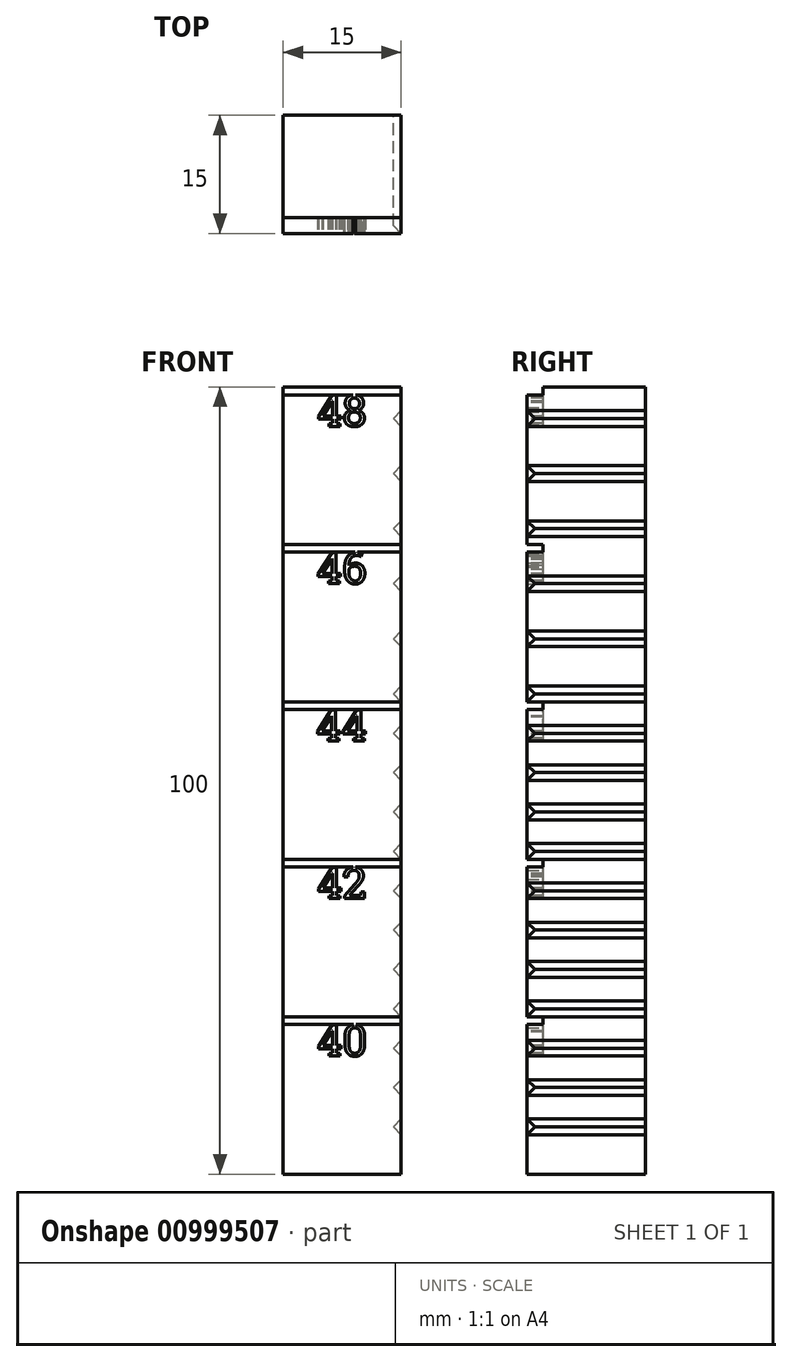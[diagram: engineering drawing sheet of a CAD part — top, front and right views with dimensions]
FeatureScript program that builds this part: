
annotation { "Feature Type Name" : "Feature", "Feature Type Description" : "" }
export const myFeature = defineFeature(function(context is Context, id is Id, definition is map)
    precondition{}
    {
        {
            var Q0;
            Q0=qCreatedBy(makeId("Top.planeOp"),FACE);
            var sketch = newSketch(context, id + "F0", { "sketchPlane" : qUnion([Q0])});
            skLineSegment(sketch, "E0.bottom", {"start": v(7.5, 7.5) * mm, "end": v(-7.5, 7.5) * mm});
            skLineSegment(sketch, "E0.top", {"start": v(7.5, -7.5) * mm, "end": v(-7.5, -7.5) * mm});
            skLineSegment(sketch, "E0.left", {"start": v(7.5, 7.5) * mm, "end": v(7.5, -7.5) * mm});
            skLineSegment(sketch, "E0.right", {"start": v(-7.5, 7.5) * mm, "end": v(-7.5, -7.5) * mm});
            skPoint(sketch, "E0.middle", {"position": v(0, 0) * mm});
            skSolve(sketch);
        }
        {
            var Q0;
            Q0=makeQuery(id+"F0.imprint","IMPRINT",FACE,{"disambiguationData":[TD([[makeQuery(id+"F0.imprint","IMPRINT",EDGE,{"derivedFrom":sQuery(id+"F0.wireOp",EDGE,"E0.bottom")}),1.0]])]});
            extrude(context, id + "F1", {"entities" : qUnion([Q0]), "depth" : 100 * mm, "offsetDistance" : 25 * mm});
        }
        {
            var Q0;
            Q0=makeQuery(id+"F1.opExtrude","SWEPT_FACE",FACE,{"disambiguationData":[OSD([sQuery(id+"F0.wireOp",EDGE,"E0.top")])]});
            var sketch = newSketch(context, id + "F2", { "sketchPlane" : qUnion([Q0])});
            skLineSegment(sketch, "E1", {"start": v(-25.16, 19) * mm, "end": v(21.74, 19) * mm});
            skLineSegment(sketch, "E2", {"start": v(-25.16, 20) * mm, "end": v(21.74, 20) * mm});
            skLineSegment(sketch, "E3", {"start": v(-25.16, 20) * mm, "end": v(-25.16, 19) * mm});
            skLineSegment(sketch, "E4", {"start": v(21.74, 20) * mm, "end": v(21.74, 19) * mm});
            skLineSegment(sketch, "E5.0.1.0", {"start": v(-25.16, 40) * mm, "end": v(21.74, 40) * mm});
            skLineSegment(sketch, "E5.0.1.1", {"start": v(-25.16, 40) * mm, "end": v(-25.16, 39) * mm});
            skLineSegment(sketch, "E5.0.1.2", {"start": v(-25.16, 39) * mm, "end": v(21.74, 39) * mm});
            skLineSegment(sketch, "E5.0.1.3", {"start": v(21.74, 40) * mm, "end": v(21.74, 39) * mm});
            skLineSegment(sketch, "E5.0.2.0", {"start": v(-25.16, 60) * mm, "end": v(21.74, 60) * mm});
            skLineSegment(sketch, "E5.0.2.1", {"start": v(-25.16, 60) * mm, "end": v(-25.16, 59) * mm});
            skLineSegment(sketch, "E5.0.2.2", {"start": v(-25.16, 59) * mm, "end": v(21.74, 59) * mm});
            skLineSegment(sketch, "E5.0.2.3", {"start": v(21.74, 60) * mm, "end": v(21.74, 59) * mm});
            skLineSegment(sketch, "E5.0.3.0", {"start": v(-25.16, 80) * mm, "end": v(21.74, 80) * mm});
            skLineSegment(sketch, "E5.0.3.1", {"start": v(-25.16, 80) * mm, "end": v(-25.16, 79) * mm});
            skLineSegment(sketch, "E5.0.3.2", {"start": v(-25.16, 79) * mm, "end": v(21.74, 79) * mm});
            skLineSegment(sketch, "E5.0.3.3", {"start": v(21.74, 80) * mm, "end": v(21.74, 79) * mm});
            skLineSegment(sketch, "E5.direction1", {"start": v(-25.16, 19) * mm, "end": v(41.34, 19) * mm, "construction": true});
            skLineSegment(sketch, "E5.direction2", {"start": v(-25.16, 19) * mm, "end": v(-25.16, 39) * mm, "construction": true});
            skText(sketch, "E6", { "text": "40", "fontName": "RobotoSlab-Regular.ttf"});
            skLineSegment(sketch, "E7", {"start": v(0, 0) * mm, "end": v(0, 100) * mm, "construction": true});
            skText(sketch, "E8", { "text": "42", "fontName": "RobotoSlab-Regular.ttf"});
            skText(sketch, "E9", { "text": "44", "fontName": "RobotoSlab-Regular.ttf"});
            skText(sketch, "E10", { "text": "46", "fontName": "RobotoSlab-Regular.ttf"});
            skLineSegment(sketch, "E11.0.1.0", {"start": v(-25.16, 99) * mm, "end": v(21.74, 99) * mm});
            skLineSegment(sketch, "E11.0.1.1", {"start": v(-25.16, 100) * mm, "end": v(21.74, 100) * mm});
            skLineSegment(sketch, "E11.0.1.2", {"start": v(-25.16, 100) * mm, "end": v(-25.16, 99) * mm});
            skLineSegment(sketch, "E11.0.1.3", {"start": v(21.74, 100) * mm, "end": v(21.74, 99) * mm});
            skLineSegment(sketch, "E11.direction1", {"start": v(-25.16, 79) * mm, "end": v(63.44, 79) * mm, "construction": true});
            skLineSegment(sketch, "E11.direction2", {"start": v(-25.16, 79) * mm, "end": v(-25.16, 99) * mm, "construction": true});
            skText(sketch, "E12", { "text": "48", "fontName": "RobotoSlab-Regular.ttf"});
            const initialGuessF2  = {"E6": [-0.0032, 0.015, 1, 0, 0.004], "E8": [-0.0032, 0.035, 1, 0, 0.004], "E9": [-0.0033, 0.055, 1, 0, 0.004], "E10": [-0.00323, 0.075, 1, 0, 0.004], "E12": [-0.0032, 0.095, 1, 0, 0.004]};
            skSetInitialGuess(sketch, initialGuessF2);
            skSolve(sketch);
        }
        {
            var Q0;
            Q0=makeQuery(id+"F2.imprint","IMPRINT",FACE,{"disambiguationData":[TD([[makeQuery(id+"F2.imprint","IMPRINT",EDGE,{"derivedFrom":sQuery(id+"F2.wireOp",EDGE,"E6.sketch_text.stroke-46")}),-1.0]])]});
            var Q1;
            Q1=makeQuery(id+"F2.imprint","IMPRINT",FACE,{"disambiguationData":[TD([[makeQuery(id+"F2.imprint","IMPRINT",EDGE,{"derivedFrom":sQuery(id+"F2.wireOp",EDGE,"E6.sketch_text.stroke-23")}),-1.0]])]});
            var Q2;
            Q2=makeQuery(id+"F2.imprint","IMPRINT",FACE,{"disambiguationData":[TD([[makeQuery(id+"F2.imprint","IMPRINT",EDGE,{"derivedFrom":sQuery(id+"F2.wireOp",EDGE,"E6.sketch_text.stroke-0")}),-1.0]])]});
            var Q3;
            {var subQ0=sQuery(id+"F2.wireOp",EDGE,"E3");Q3=makeQuery(id+"F2.imprint","IMPRINT",FACE,{"disambiguationData":[TD([[makeQuery(id+"F2.imprint","IMPRINT",EDGE,{"derivedFrom":subQ0}),1.0]])]});}
            var Q4;
            {var subQ3=sQuery(id+"F2.wireOp",EDGE,"E1");var subQ10=sQuery(id+"F2.wireOp",EDGE,"E6.sketch_text.stroke-12");var subQ19=makeQuery(id+"F2.imprint","INTERSECT",VERTEX,{"derivedFrom":[subQ3,subQ10]});Q4=makeQuery(id+"F2.imprint","IMPRINT",FACE,{"disambiguationData":[TD([[makeQuery(id+"F2.imprint","IMPRINT",EDGE,{"disambiguationData":[TD([[subQ19,-1.0]])],"derivedFrom":subQ3}),1.0]])]});}
            var Q5;
            {var subQ0=sQuery(id+"F2.wireOp",EDGE,"E4");Q5=makeQuery(id+"F2.imprint","IMPRINT",FACE,{"disambiguationData":[TD([[makeQuery(id+"F2.imprint","IMPRINT",EDGE,{"derivedFrom":subQ0}),-1.0]])]});}
            var Q6;
            {var subQ0=sQuery(id+"F2.wireOp",EDGE,"E5.0.1.1");Q6=makeQuery(id+"F2.imprint","IMPRINT",FACE,{"disambiguationData":[TD([[makeQuery(id+"F2.imprint","IMPRINT",EDGE,{"derivedFrom":subQ0}),1.0]])]});}
            var Q7;
            {var subQ1=sQuery(id+"F2.wireOp",EDGE,"E5.0.1.2");var subQ9=sQuery(id+"F2.wireOp",EDGE,"E8.sketch_text.stroke-12");var subQ10=makeQuery(id+"F2.imprint","INTERSECT",VERTEX,{"derivedFrom":[subQ1,subQ9]});Q7=makeQuery(id+"F2.imprint","IMPRINT",FACE,{"disambiguationData":[TD([[makeQuery(id+"F2.imprint","IMPRINT",EDGE,{"disambiguationData":[TD([[subQ10,-1.0]])],"derivedFrom":subQ1}),1.0]])]});}
            var Q8;
            {var subQ0=sQuery(id+"F2.wireOp",EDGE,"E5.0.1.3");Q8=makeQuery(id+"F2.imprint","IMPRINT",FACE,{"disambiguationData":[TD([[makeQuery(id+"F2.imprint","IMPRINT",EDGE,{"derivedFrom":subQ0}),-1.0]])]});}
            var Q9;
            Q9=makeQuery(id+"F2.imprint","IMPRINT",FACE,{"disambiguationData":[TD([[makeQuery(id+"F2.imprint","IMPRINT",EDGE,{"derivedFrom":sQuery(id+"F2.wireOp",EDGE,"E8.sketch_text.stroke-33")}),-1.0]])]});
            var Q10;
            Q10=makeQuery(id+"F2.imprint","IMPRINT",FACE,{"disambiguationData":[TD([[makeQuery(id+"F2.imprint","IMPRINT",EDGE,{"derivedFrom":sQuery(id+"F2.wireOp",EDGE,"E8.sketch_text.stroke-23")}),-1.0]])]});
            var Q11;
            Q11=makeQuery(id+"F2.imprint","IMPRINT",FACE,{"disambiguationData":[TD([[makeQuery(id+"F2.imprint","IMPRINT",EDGE,{"derivedFrom":sQuery(id+"F2.wireOp",EDGE,"E8.sketch_text.stroke-0")}),-1.0]])]});
            var Q12;
            {var subQ0=sQuery(id+"F2.wireOp",EDGE,"E9.sketch_text.stroke-12");var subQ3=sQuery(id+"F2.wireOp",EDGE,"E5.0.2.2");var subQ4=makeQuery(id+"F2.imprint","INTERSECT",VERTEX,{"derivedFrom":[subQ3,subQ0]});Q12=makeQuery(id+"F2.imprint","IMPRINT",FACE,{"disambiguationData":[TD([[makeQuery(id+"F2.imprint","IMPRINT",EDGE,{"disambiguationData":[TD([[subQ4,-1.0]])],"derivedFrom":subQ3}),1.0]])]});}
            var Q13;
            {var subQ0=sQuery(id+"F2.wireOp",EDGE,"E5.0.2.3");Q13=makeQuery(id+"F2.imprint","IMPRINT",FACE,{"disambiguationData":[TD([[makeQuery(id+"F2.imprint","IMPRINT",EDGE,{"derivedFrom":subQ0}),-1.0]])]});}
            var Q14;
            {var subQ0=sQuery(id+"F2.wireOp",EDGE,"E5.0.2.1");Q14=makeQuery(id+"F2.imprint","IMPRINT",FACE,{"disambiguationData":[TD([[makeQuery(id+"F2.imprint","IMPRINT",EDGE,{"derivedFrom":subQ0}),1.0]])]});}
            var Q15;
            Q15=makeQuery(id+"F2.imprint","IMPRINT",FACE,{"disambiguationData":[TD([[makeQuery(id+"F2.imprint","IMPRINT",EDGE,{"derivedFrom":sQuery(id+"F2.wireOp",EDGE,"E9.sketch_text.stroke-0")}),-1.0]])]});
            var Q16;
            Q16=makeQuery(id+"F2.imprint","IMPRINT",FACE,{"disambiguationData":[TD([[makeQuery(id+"F2.imprint","IMPRINT",EDGE,{"derivedFrom":sQuery(id+"F2.wireOp",EDGE,"E9.sketch_text.stroke-23")}),-1.0]])]});
            var Q17;
            Q17=makeQuery(id+"F2.imprint","IMPRINT",FACE,{"disambiguationData":[TD([[makeQuery(id+"F2.imprint","IMPRINT",EDGE,{"derivedFrom":sQuery(id+"F2.wireOp",EDGE,"E9.sketch_text.stroke-43")}),-1.0]])]});
            var Q18;
            {var subQ1=sQuery(id+"F2.wireOp",EDGE,"E5.0.3.2");var subQ6=sQuery(id+"F2.wireOp",EDGE,"E10.sketch_text.stroke-19");var subQ10=makeQuery(id+"F2.imprint","INTERSECT",VERTEX,{"derivedFrom":[subQ1,subQ6]});Q18=makeQuery(id+"F2.imprint","IMPRINT",FACE,{"disambiguationData":[TD([[makeQuery(id+"F2.imprint","IMPRINT",EDGE,{"disambiguationData":[TD([[subQ10,-1.0]])],"derivedFrom":subQ1}),1.0]])]});}
            var Q19;
            {var subQ3=sQuery(id+"F2.wireOp",EDGE,"E5.0.3.3");Q19=makeQuery(id+"F2.imprint","IMPRINT",FACE,{"disambiguationData":[TD([[makeQuery(id+"F2.imprint","IMPRINT",EDGE,{"derivedFrom":subQ3}),-1.0]])]});}
            var Q20;
            {var subQ3=sQuery(id+"F2.wireOp",EDGE,"E5.0.3.1");Q20=makeQuery(id+"F2.imprint","IMPRINT",FACE,{"disambiguationData":[TD([[makeQuery(id+"F2.imprint","IMPRINT",EDGE,{"derivedFrom":subQ3}),1.0]])]});}
            var Q21;
            Q21=makeQuery(id+"F2.imprint","IMPRINT",FACE,{"disambiguationData":[TD([[makeQuery(id+"F2.imprint","IMPRINT",EDGE,{"derivedFrom":sQuery(id+"F2.wireOp",EDGE,"E10.sketch_text.stroke-38")}),-1.0]])]});
            var Q22;
            {var subQ6=sQuery(id+"F2.wireOp",EDGE,"E8.sketch_text.stroke-50");Q22=makeQuery(id+"F2.imprint","IMPRINT",FACE,{"disambiguationData":[TD([[makeQuery(id+"F2.imprint","IMPRINT",EDGE,{"derivedFrom":subQ6}),-1.0]])]});}
            var Q23;
            Q23=makeQuery(id+"F2.imprint","IMPRINT",FACE,{"disambiguationData":[TD([[makeQuery(id+"F2.imprint","IMPRINT",EDGE,{"derivedFrom":sQuery(id+"F2.wireOp",EDGE,"E8.sketch_text.stroke-90")}),-1.0]])]});
            var Q24;
            Q24=makeQuery(id+"F2.imprint","IMPRINT",FACE,{"disambiguationData":[TD([[makeQuery(id+"F2.imprint","IMPRINT",EDGE,{"derivedFrom":sQuery(id+"F2.wireOp",EDGE,"E8.sketch_text.stroke-70")}),-1.0]])]});
            var Q25;
            {var subQ6=sQuery(id+"F2.wireOp",EDGE,"E6.sketch_text.stroke-56");Q25=makeQuery(id+"F2.imprint","IMPRINT",FACE,{"disambiguationData":[TD([[makeQuery(id+"F2.imprint","IMPRINT",EDGE,{"derivedFrom":subQ6}),-1.0]])]});}
            var Q26;
            Q26=makeQuery(id+"F2.imprint","IMPRINT",FACE,{"disambiguationData":[TD([[makeQuery(id+"F2.imprint","IMPRINT",EDGE,{"derivedFrom":sQuery(id+"F2.wireOp",EDGE,"E6.sketch_text.stroke-96")}),-1.0]])]});
            var Q27;
            Q27=makeQuery(id+"F2.imprint","IMPRINT",FACE,{"disambiguationData":[TD([[makeQuery(id+"F2.imprint","IMPRINT",EDGE,{"derivedFrom":sQuery(id+"F2.wireOp",EDGE,"E6.sketch_text.stroke-76")}),-1.0]])]});
            var Q28;
            {var subQ6=sQuery(id+"F2.wireOp",EDGE,"E9.sketch_text.stroke-54");Q28=makeQuery(id+"F2.imprint","IMPRINT",FACE,{"disambiguationData":[TD([[makeQuery(id+"F2.imprint","IMPRINT",EDGE,{"derivedFrom":subQ6}),-1.0]])]});}
            var Q29;
            Q29=makeQuery(id+"F2.imprint","IMPRINT",FACE,{"disambiguationData":[TD([[makeQuery(id+"F2.imprint","IMPRINT",EDGE,{"derivedFrom":sQuery(id+"F2.wireOp",EDGE,"E9.sketch_text.stroke-94")}),-1.0]])]});
            var Q30;
            Q30=makeQuery(id+"F2.imprint","IMPRINT",FACE,{"disambiguationData":[TD([[makeQuery(id+"F2.imprint","IMPRINT",EDGE,{"derivedFrom":sQuery(id+"F2.wireOp",EDGE,"E9.sketch_text.stroke-74")}),-1.0]])]});
            var Q31;
            {var subQ6=sQuery(id+"F2.wireOp",EDGE,"E10.sketch_text.stroke-48");Q31=makeQuery(id+"F2.imprint","IMPRINT",FACE,{"disambiguationData":[TD([[makeQuery(id+"F2.imprint","IMPRINT",EDGE,{"derivedFrom":subQ6}),-1.0]])]});}
            var Q32;
            Q32=makeQuery(id+"F2.imprint","IMPRINT",FACE,{"disambiguationData":[TD([[makeQuery(id+"F2.imprint","IMPRINT",EDGE,{"derivedFrom":sQuery(id+"F2.wireOp",EDGE,"E10.sketch_text.stroke-88")}),-1.0]])]});
            var Q33;
            Q33=makeQuery(id+"F2.imprint","IMPRINT",FACE,{"disambiguationData":[TD([[makeQuery(id+"F2.imprint","IMPRINT",EDGE,{"derivedFrom":sQuery(id+"F2.wireOp",EDGE,"E10.sketch_text.stroke-68")}),-1.0]])]});
            var Q34;
            {var subQ0=sQuery(id+"F2.wireOp",EDGE,"E11.0.1.2");Q34=makeQuery(id+"F2.imprint","IMPRINT",FACE,{"disambiguationData":[TD([[makeQuery(id+"F2.imprint","IMPRINT",EDGE,{"derivedFrom":subQ0}),1.0]])]});}
            var Q35;
            {var subQ1=sQuery(id+"F2.wireOp",EDGE,"E11.0.1.0");var subQ6=sQuery(id+"F2.wireOp",EDGE,"E12.sketch_text.stroke-14");var subQ9=makeQuery(id+"F2.imprint","INTERSECT",VERTEX,{"derivedFrom":[subQ1,subQ6]});Q35=makeQuery(id+"F2.imprint","IMPRINT",FACE,{"disambiguationData":[TD([[makeQuery(id+"F2.imprint","IMPRINT",EDGE,{"disambiguationData":[TD([[subQ9,-1.0]])],"derivedFrom":subQ1}),1.0]])]});}
            var Q36;
            {var subQ0=sQuery(id+"F2.wireOp",EDGE,"E11.0.1.3");Q36=makeQuery(id+"F2.imprint","IMPRINT",FACE,{"disambiguationData":[TD([[makeQuery(id+"F2.imprint","IMPRINT",EDGE,{"derivedFrom":subQ0}),-1.0]])]});}
            var Q37;
            Q37=makeQuery(id+"F2.imprint","IMPRINT",FACE,{"disambiguationData":[TD([[makeQuery(id+"F2.imprint","IMPRINT",EDGE,{"derivedFrom":sQuery(id+"F2.wireOp",EDGE,"E12.sketch_text.stroke-0")}),-1.0]])]});
            var Q38;
            Q38=makeQuery(id+"F2.imprint","IMPRINT",FACE,{"disambiguationData":[TD([[makeQuery(id+"F2.imprint","IMPRINT",EDGE,{"derivedFrom":sQuery(id+"F2.wireOp",EDGE,"E12.sketch_text.stroke-32")}),-1.0]])]});
            var Q39;
            {var subQ6=sQuery(id+"F2.wireOp",EDGE,"E12.sketch_text.stroke-58");Q39=makeQuery(id+"F2.imprint","IMPRINT",FACE,{"disambiguationData":[TD([[makeQuery(id+"F2.imprint","IMPRINT",EDGE,{"derivedFrom":subQ6}),-1.0]])]});}
            var Q40;
            Q40=makeQuery(id+"F2.imprint","IMPRINT",FACE,{"disambiguationData":[TD([[makeQuery(id+"F2.imprint","IMPRINT",EDGE,{"derivedFrom":sQuery(id+"F2.wireOp",EDGE,"E12.sketch_text.stroke-98")}),-1.0]])]});
            var Q41;
            Q41=makeQuery(id+"F2.imprint","IMPRINT",FACE,{"disambiguationData":[TD([[makeQuery(id+"F2.imprint","IMPRINT",EDGE,{"derivedFrom":sQuery(id+"F2.wireOp",EDGE,"E12.sketch_text.stroke-78")}),-1.0]])]});
            var Q42;
            {var subQ6=sQuery(id+"F2.wireOp",EDGE,"E10.sketch_text.stroke-21");Q42=makeQuery(id+"F2.imprint","IMPRINT",FACE,{"disambiguationData":[TD([[makeQuery(id+"F2.imprint","IMPRINT",EDGE,{"derivedFrom":subQ6}),-1.0]])]});}
            var Q43;
            Q43=makeQuery(id+"F2.imprint","IMPRINT",FACE,{"disambiguationData":[TD([[makeQuery(id+"F2.imprint","IMPRINT",EDGE,{"derivedFrom":sQuery(id+"F2.wireOp",EDGE,"E10.sketch_text.stroke-0")}),-1.0]])]});
            extrude(context, id + "F3", {"entities" : qUnion([Q0, Q1, Q2, Q3, Q4, Q5, Q6, Q7, Q8, Q9, Q10, Q11, Q12, Q13, Q14, Q15, Q16, Q17, Q18, Q19, Q20, Q21, Q22, Q23, Q24, Q25, Q26, Q27, Q28, Q29, Q30, Q31, Q32, Q33, Q34, Q35, Q36, Q37, Q38, Q39, Q40, Q41, Q42, Q43]), "operationType" : NewBodyOperationType.REMOVE, "oppositeDirection" : true, "depth" : 2 * mm, "offsetDistance" : 25 * mm, "hasDraft" : true, "draftAngle" : 0 * degree});
        }
        {
            var Q0;
            Q0=makeQuery(id+"F1.opExtrude","SWEPT_FACE",FACE,{"disambiguationData":[OSD([sQuery(id+"F0.wireOp",EDGE,"E0.left")])]});
            var sketch = newSketch(context, id + "F4", { "sketchPlane" : qUnion([Q0])});
            skLineSegment(sketch, "E13", {"start": v(0, 0) * mm, "end": v(0, 167.33) * mm, "construction": true});
            skLineSegment(sketch, "E14.bottom", {"start": v(-19.55, 7) * mm, "end": v(25.45, 7) * mm});
            skLineSegment(sketch, "E14.top", {"start": v(-19.55, 5) * mm, "end": v(25.45, 5) * mm});
            skLineSegment(sketch, "E14.left", {"start": v(-19.55, 7) * mm, "end": v(-19.55, 5) * mm});
            skLineSegment(sketch, "E14.right", {"start": v(25.45, 7) * mm, "end": v(25.45, 5) * mm});
            skLineSegment(sketch, "E15.0.1.0", {"start": v(-19.55, 12) * mm, "end": v(-19.55, 10) * mm});
            skLineSegment(sketch, "E15.0.1.1", {"start": v(-19.55, 12) * mm, "end": v(25.45, 12) * mm});
            skLineSegment(sketch, "E15.0.1.2", {"start": v(-19.55, 10) * mm, "end": v(25.45, 10) * mm});
            skLineSegment(sketch, "E15.0.1.3", {"start": v(25.45, 12) * mm, "end": v(25.45, 10) * mm});
            skLineSegment(sketch, "E15.0.2.0", {"start": v(-19.55, 17) * mm, "end": v(-19.55, 15) * mm});
            skLineSegment(sketch, "E15.0.2.1", {"start": v(-19.55, 17) * mm, "end": v(25.45, 17) * mm});
            skLineSegment(sketch, "E15.0.2.2", {"start": v(-19.55, 15) * mm, "end": v(25.45, 15) * mm});
            skLineSegment(sketch, "E15.0.2.3", {"start": v(25.45, 17) * mm, "end": v(25.45, 15) * mm});
            skLineSegment(sketch, "E15.0.3.0", {"start": v(-19.55, 22) * mm, "end": v(-19.55, 20) * mm});
            skLineSegment(sketch, "E15.0.3.1", {"start": v(-19.55, 22) * mm, "end": v(25.45, 22) * mm});
            skLineSegment(sketch, "E15.0.3.2", {"start": v(-19.55, 20) * mm, "end": v(25.45, 20) * mm});
            skLineSegment(sketch, "E15.0.3.3", {"start": v(25.45, 22) * mm, "end": v(25.45, 20) * mm});
            skLineSegment(sketch, "E15.0.4.0", {"start": v(-19.55, 27) * mm, "end": v(-19.55, 25) * mm});
            skLineSegment(sketch, "E15.0.4.1", {"start": v(-19.55, 27) * mm, "end": v(25.45, 27) * mm});
            skLineSegment(sketch, "E15.0.4.2", {"start": v(-19.55, 25) * mm, "end": v(25.45, 25) * mm});
            skLineSegment(sketch, "E15.0.4.3", {"start": v(25.45, 27) * mm, "end": v(25.45, 25) * mm});
            skLineSegment(sketch, "E15.0.5.0", {"start": v(-19.55, 32) * mm, "end": v(-19.55, 30) * mm});
            skLineSegment(sketch, "E15.0.5.1", {"start": v(-19.55, 32) * mm, "end": v(25.45, 32) * mm});
            skLineSegment(sketch, "E15.0.5.2", {"start": v(-19.55, 30) * mm, "end": v(25.45, 30) * mm});
            skLineSegment(sketch, "E15.0.5.3", {"start": v(25.45, 32) * mm, "end": v(25.45, 30) * mm});
            skLineSegment(sketch, "E15.0.6.0", {"start": v(-19.55, 37) * mm, "end": v(-19.55, 35) * mm});
            skLineSegment(sketch, "E15.0.6.1", {"start": v(-19.55, 37) * mm, "end": v(25.45, 37) * mm});
            skLineSegment(sketch, "E15.0.6.2", {"start": v(-19.55, 35) * mm, "end": v(25.45, 35) * mm});
            skLineSegment(sketch, "E15.0.6.3", {"start": v(25.45, 37) * mm, "end": v(25.45, 35) * mm});
            skLineSegment(sketch, "E15.0.7.0", {"start": v(-19.55, 42) * mm, "end": v(-19.55, 40) * mm});
            skLineSegment(sketch, "E15.0.7.1", {"start": v(-19.55, 42) * mm, "end": v(25.45, 42) * mm});
            skLineSegment(sketch, "E15.0.7.2", {"start": v(-19.55, 40) * mm, "end": v(25.45, 40) * mm});
            skLineSegment(sketch, "E15.0.7.3", {"start": v(25.45, 42) * mm, "end": v(25.45, 40) * mm});
            skLineSegment(sketch, "E15.0.8.0", {"start": v(-19.55, 47) * mm, "end": v(-19.55, 45) * mm});
            skLineSegment(sketch, "E15.0.8.1", {"start": v(-19.55, 47) * mm, "end": v(25.45, 47) * mm});
            skLineSegment(sketch, "E15.0.8.2", {"start": v(-19.55, 45) * mm, "end": v(25.45, 45) * mm});
            skLineSegment(sketch, "E15.0.8.3", {"start": v(25.45, 47) * mm, "end": v(25.45, 45) * mm});
            skLineSegment(sketch, "E15.0.9.0", {"start": v(-19.55, 52) * mm, "end": v(-19.55, 50) * mm});
            skLineSegment(sketch, "E15.0.9.1", {"start": v(-19.55, 52) * mm, "end": v(25.45, 52) * mm});
            skLineSegment(sketch, "E15.0.9.2", {"start": v(-19.55, 50) * mm, "end": v(25.45, 50) * mm});
            skLineSegment(sketch, "E15.0.9.3", {"start": v(25.45, 52) * mm, "end": v(25.45, 50) * mm});
            skLineSegment(sketch, "E15.0.10.0", {"start": v(-19.55, 57) * mm, "end": v(-19.55, 55) * mm});
            skLineSegment(sketch, "E15.0.10.1", {"start": v(-19.55, 57) * mm, "end": v(25.45, 57) * mm});
            skLineSegment(sketch, "E15.0.10.2", {"start": v(-19.55, 55) * mm, "end": v(25.45, 55) * mm});
            skLineSegment(sketch, "E15.0.10.3", {"start": v(25.45, 57) * mm, "end": v(25.45, 55) * mm});
            skLineSegment(sketch, "E15.0.11.0", {"start": v(-19.55, 62) * mm, "end": v(-19.55, 60) * mm});
            skLineSegment(sketch, "E15.0.11.1", {"start": v(-19.55, 62) * mm, "end": v(25.45, 62) * mm});
            skLineSegment(sketch, "E15.0.11.2", {"start": v(-19.55, 60) * mm, "end": v(25.45, 60) * mm});
            skLineSegment(sketch, "E15.0.11.3", {"start": v(25.45, 62) * mm, "end": v(25.45, 60) * mm});
            skLineSegment(sketch, "E15.direction1", {"start": v(-19.55, 5) * mm, "end": v(5.45, 5) * mm, "construction": true});
            skLineSegment(sketch, "E15.direction2", {"start": v(-19.55, 5) * mm, "end": v(-19.55, 10) * mm, "construction": true});
            skLineSegment(sketch, "E16.0.1.0", {"start": v(-19.55, 67) * mm, "end": v(25.45, 67) * mm});
            skLineSegment(sketch, "E16.0.1.1", {"start": v(-19.55, 69) * mm, "end": v(25.45, 69) * mm});
            skLineSegment(sketch, "E16.0.1.2", {"start": v(-19.55, 69) * mm, "end": v(-19.55, 67) * mm});
            skLineSegment(sketch, "E16.0.1.3", {"start": v(25.45, 69) * mm, "end": v(25.45, 67) * mm});
            skLineSegment(sketch, "E16.0.2.0", {"start": v(-19.55, 74) * mm, "end": v(25.45, 74) * mm});
            skLineSegment(sketch, "E16.0.2.1", {"start": v(-19.55, 76) * mm, "end": v(25.45, 76) * mm});
            skLineSegment(sketch, "E16.0.2.2", {"start": v(-19.55, 76) * mm, "end": v(-19.55, 74) * mm});
            skLineSegment(sketch, "E16.0.2.3", {"start": v(25.45, 76) * mm, "end": v(25.45, 74) * mm});
            skLineSegment(sketch, "E16.direction1", {"start": v(-19.55, 60) * mm, "end": v(5.45, 60) * mm, "construction": true});
            skLineSegment(sketch, "E16.direction2", {"start": v(-19.55, 60) * mm, "end": v(-19.55, 67) * mm, "construction": true});
            skLineSegment(sketch, "E17.0.1.0", {"start": v(-19.55, 83) * mm, "end": v(25.45, 83) * mm});
            skLineSegment(sketch, "E17.0.1.1", {"start": v(25.45, 83) * mm, "end": v(25.45, 81) * mm});
            skLineSegment(sketch, "E17.0.1.2", {"start": v(-19.55, 81) * mm, "end": v(25.45, 81) * mm});
            skLineSegment(sketch, "E17.0.1.3", {"start": v(-19.55, 83) * mm, "end": v(-19.55, 81) * mm});
            skLineSegment(sketch, "E17.0.2.0", {"start": v(-19.55, 90) * mm, "end": v(25.45, 90) * mm});
            skLineSegment(sketch, "E17.0.2.1", {"start": v(25.45, 90) * mm, "end": v(25.45, 88) * mm});
            skLineSegment(sketch, "E17.0.2.2", {"start": v(-19.55, 88) * mm, "end": v(25.45, 88) * mm});
            skLineSegment(sketch, "E17.0.2.3", {"start": v(-19.55, 90) * mm, "end": v(-19.55, 88) * mm});
            skLineSegment(sketch, "E17.0.3.0", {"start": v(-19.55, 97) * mm, "end": v(25.45, 97) * mm});
            skLineSegment(sketch, "E17.0.3.1", {"start": v(25.45, 97) * mm, "end": v(25.45, 95) * mm});
            skLineSegment(sketch, "E17.0.3.2", {"start": v(-19.55, 95) * mm, "end": v(25.45, 95) * mm});
            skLineSegment(sketch, "E17.0.3.3", {"start": v(-19.55, 97) * mm, "end": v(-19.55, 95) * mm});
            skLineSegment(sketch, "E17.direction1", {"start": v(-19.55, 74) * mm, "end": v(39.95, 74) * mm, "construction": true});
            skLineSegment(sketch, "E17.direction2", {"start": v(-19.55, 74) * mm, "end": v(-19.55, 81) * mm, "construction": true});
            skSolve(sketch);
        }
        {
            var Q0;
            {var subQ0=sQuery(id+"F4.wireOp",EDGE,"E16.0.2.3");Q0=makeQuery(id+"F4.imprint","IMPRINT",FACE,{"disambiguationData":[TD([[makeQuery(id+"F4.imprint","IMPRINT",EDGE,{"derivedFrom":subQ0}),-1.0]])]});}
            var Q1;
            {var subQ0=sQuery(id+"F4.wireOp",EDGE,"E16.0.2.0");var subQ2=sQuery(id+"F0.wireOp",EDGE,"E0.left");var subQ8=makeQuery(id+"F1.opExtrude","SWEPT_EDGE",EDGE,{"disambiguationData":[OSD([sQuery(id+"F0.wireOp",EDGE,"E0.bottom"),subQ2])]});var subQ9=makeQuery(id+"F4.imprint","INTERSECT",VERTEX,{"derivedFrom":[subQ8,subQ0]});Q1=makeQuery(id+"F4.imprint","IMPRINT",FACE,{"disambiguationData":[TD([[makeQuery(id+"F4.imprint","IMPRINT",EDGE,{"disambiguationData":[TD([[subQ9,1.0]])],"derivedFrom":subQ8}),-1.0]])]});}
            var Q2;
            {var subQ0=sQuery(id+"F4.wireOp",EDGE,"E16.0.1.3");Q2=makeQuery(id+"F4.imprint","IMPRINT",FACE,{"disambiguationData":[TD([[makeQuery(id+"F4.imprint","IMPRINT",EDGE,{"derivedFrom":subQ0}),-1.0]])]});}
            var Q3;
            {var subQ0=sQuery(id+"F4.wireOp",EDGE,"E16.0.1.0");var subQ2=sQuery(id+"F0.wireOp",EDGE,"E0.left");var subQ8=makeQuery(id+"F1.opExtrude","SWEPT_EDGE",EDGE,{"disambiguationData":[OSD([sQuery(id+"F0.wireOp",EDGE,"E0.bottom"),subQ2])]});var subQ9=makeQuery(id+"F4.imprint","INTERSECT",VERTEX,{"derivedFrom":[subQ8,subQ0]});Q3=makeQuery(id+"F4.imprint","IMPRINT",FACE,{"disambiguationData":[TD([[makeQuery(id+"F4.imprint","IMPRINT",EDGE,{"disambiguationData":[TD([[subQ9,1.0]])],"derivedFrom":subQ8}),-1.0]])]});}
            var Q4;
            {var subQ0=sQuery(id+"F4.wireOp",EDGE,"E15.0.11.3");Q4=makeQuery(id+"F4.imprint","IMPRINT",FACE,{"disambiguationData":[TD([[makeQuery(id+"F4.imprint","IMPRINT",EDGE,{"derivedFrom":subQ0}),-1.0]])]});}
            var Q5;
            {var subQ0=sQuery(id+"F4.wireOp",EDGE,"E15.0.11.1");var subQ2=sQuery(id+"F0.wireOp",EDGE,"E0.left");var subQ10=makeQuery(id+"F1.opExtrude","SWEPT_EDGE",EDGE,{"disambiguationData":[OSD([sQuery(id+"F0.wireOp",EDGE,"E0.bottom"),subQ2])]});var subQ11=makeQuery(id+"F4.imprint","INTERSECT",VERTEX,{"derivedFrom":[subQ10,subQ0]});Q5=makeQuery(id+"F4.imprint","IMPRINT",FACE,{"disambiguationData":[TD([[makeQuery(id+"F4.imprint","IMPRINT",EDGE,{"disambiguationData":[TD([[subQ11,-1.0]])],"derivedFrom":subQ10}),-1.0]])]});}
            var Q6;
            {var subQ0=sQuery(id+"F4.wireOp",EDGE,"E15.0.10.3");Q6=makeQuery(id+"F4.imprint","IMPRINT",FACE,{"disambiguationData":[TD([[makeQuery(id+"F4.imprint","IMPRINT",EDGE,{"derivedFrom":subQ0}),-1.0]])]});}
            var Q7;
            {var subQ0=sQuery(id+"F4.wireOp",EDGE,"E15.0.10.1");var subQ2=sQuery(id+"F0.wireOp",EDGE,"E0.left");var subQ8=makeQuery(id+"F1.opExtrude","SWEPT_EDGE",EDGE,{"disambiguationData":[OSD([sQuery(id+"F0.wireOp",EDGE,"E0.bottom"),subQ2])]});var subQ9=makeQuery(id+"F4.imprint","INTERSECT",VERTEX,{"derivedFrom":[subQ8,subQ0]});Q7=makeQuery(id+"F4.imprint","IMPRINT",FACE,{"disambiguationData":[TD([[makeQuery(id+"F4.imprint","IMPRINT",EDGE,{"disambiguationData":[TD([[subQ9,-1.0]])],"derivedFrom":subQ8}),-1.0]])]});}
            var Q8;
            {var subQ0=sQuery(id+"F4.wireOp",EDGE,"E15.0.9.1");var subQ2=sQuery(id+"F0.wireOp",EDGE,"E0.left");var subQ8=makeQuery(id+"F1.opExtrude","SWEPT_EDGE",EDGE,{"disambiguationData":[OSD([sQuery(id+"F0.wireOp",EDGE,"E0.bottom"),subQ2])]});var subQ9=makeQuery(id+"F4.imprint","INTERSECT",VERTEX,{"derivedFrom":[subQ8,subQ0]});Q8=makeQuery(id+"F4.imprint","IMPRINT",FACE,{"disambiguationData":[TD([[makeQuery(id+"F4.imprint","IMPRINT",EDGE,{"disambiguationData":[TD([[subQ9,-1.0]])],"derivedFrom":subQ8}),-1.0]])]});}
            var Q9;
            {var subQ0=sQuery(id+"F4.wireOp",EDGE,"E15.0.9.3");Q9=makeQuery(id+"F4.imprint","IMPRINT",FACE,{"disambiguationData":[TD([[makeQuery(id+"F4.imprint","IMPRINT",EDGE,{"derivedFrom":subQ0}),-1.0]])]});}
            var Q10;
            {var subQ0=sQuery(id+"F4.wireOp",EDGE,"E15.0.8.1");var subQ2=sQuery(id+"F0.wireOp",EDGE,"E0.left");var subQ8=makeQuery(id+"F1.opExtrude","SWEPT_EDGE",EDGE,{"disambiguationData":[OSD([sQuery(id+"F0.wireOp",EDGE,"E0.bottom"),subQ2])]});var subQ9=makeQuery(id+"F4.imprint","INTERSECT",VERTEX,{"derivedFrom":[subQ8,subQ0]});Q10=makeQuery(id+"F4.imprint","IMPRINT",FACE,{"disambiguationData":[TD([[makeQuery(id+"F4.imprint","IMPRINT",EDGE,{"disambiguationData":[TD([[subQ9,-1.0]])],"derivedFrom":subQ8}),-1.0]])]});}
            var Q11;
            {var subQ0=sQuery(id+"F4.wireOp",EDGE,"E15.0.8.3");Q11=makeQuery(id+"F4.imprint","IMPRINT",FACE,{"disambiguationData":[TD([[makeQuery(id+"F4.imprint","IMPRINT",EDGE,{"derivedFrom":subQ0}),-1.0]])]});}
            var Q12;
            {var subQ0=sQuery(id+"F4.wireOp",EDGE,"E15.0.7.3");Q12=makeQuery(id+"F4.imprint","IMPRINT",FACE,{"disambiguationData":[TD([[makeQuery(id+"F4.imprint","IMPRINT",EDGE,{"derivedFrom":subQ0}),-1.0]])]});}
            var Q13;
            {var subQ0=sQuery(id+"F4.wireOp",EDGE,"E15.0.7.1");var subQ2=sQuery(id+"F0.wireOp",EDGE,"E0.left");var subQ10=makeQuery(id+"F1.opExtrude","SWEPT_EDGE",EDGE,{"disambiguationData":[OSD([sQuery(id+"F0.wireOp",EDGE,"E0.bottom"),subQ2])]});var subQ11=makeQuery(id+"F4.imprint","INTERSECT",VERTEX,{"derivedFrom":[subQ10,subQ0]});Q13=makeQuery(id+"F4.imprint","IMPRINT",FACE,{"disambiguationData":[TD([[makeQuery(id+"F4.imprint","IMPRINT",EDGE,{"disambiguationData":[TD([[subQ11,-1.0]])],"derivedFrom":subQ10}),-1.0]])]});}
            var Q14;
            {var subQ0=sQuery(id+"F4.wireOp",EDGE,"E15.0.6.3");Q14=makeQuery(id+"F4.imprint","IMPRINT",FACE,{"disambiguationData":[TD([[makeQuery(id+"F4.imprint","IMPRINT",EDGE,{"derivedFrom":subQ0}),-1.0]])]});}
            var Q15;
            {var subQ0=sQuery(id+"F4.wireOp",EDGE,"E15.0.6.1");var subQ3=sQuery(id+"F0.wireOp",EDGE,"E0.left");var subQ8=makeQuery(id+"F1.opExtrude","SWEPT_EDGE",EDGE,{"disambiguationData":[OSD([sQuery(id+"F0.wireOp",EDGE,"E0.bottom"),subQ3])]});var subQ9=makeQuery(id+"F4.imprint","INTERSECT",VERTEX,{"derivedFrom":[subQ8,subQ0]});Q15=makeQuery(id+"F4.imprint","IMPRINT",FACE,{"disambiguationData":[TD([[makeQuery(id+"F4.imprint","IMPRINT",EDGE,{"disambiguationData":[TD([[subQ9,-1.0]])],"derivedFrom":subQ8}),-1.0]])]});}
            var Q16;
            {var subQ0=sQuery(id+"F4.wireOp",EDGE,"E15.0.5.3");Q16=makeQuery(id+"F4.imprint","IMPRINT",FACE,{"disambiguationData":[TD([[makeQuery(id+"F4.imprint","IMPRINT",EDGE,{"derivedFrom":subQ0}),-1.0]])]});}
            var Q17;
            {var subQ0=sQuery(id+"F4.wireOp",EDGE,"E15.0.5.1");var subQ3=sQuery(id+"F0.wireOp",EDGE,"E0.left");var subQ8=makeQuery(id+"F1.opExtrude","SWEPT_EDGE",EDGE,{"disambiguationData":[OSD([sQuery(id+"F0.wireOp",EDGE,"E0.bottom"),subQ3])]});var subQ9=makeQuery(id+"F4.imprint","INTERSECT",VERTEX,{"derivedFrom":[subQ8,subQ0]});Q17=makeQuery(id+"F4.imprint","IMPRINT",FACE,{"disambiguationData":[TD([[makeQuery(id+"F4.imprint","IMPRINT",EDGE,{"disambiguationData":[TD([[subQ9,-1.0]])],"derivedFrom":subQ8}),-1.0]])]});}
            var Q18;
            {var subQ0=sQuery(id+"F4.wireOp",EDGE,"E15.0.4.1");var subQ3=sQuery(id+"F0.wireOp",EDGE,"E0.left");var subQ8=makeQuery(id+"F1.opExtrude","SWEPT_EDGE",EDGE,{"disambiguationData":[OSD([sQuery(id+"F0.wireOp",EDGE,"E0.bottom"),subQ3])]});var subQ9=makeQuery(id+"F4.imprint","INTERSECT",VERTEX,{"derivedFrom":[subQ8,subQ0]});Q18=makeQuery(id+"F4.imprint","IMPRINT",FACE,{"disambiguationData":[TD([[makeQuery(id+"F4.imprint","IMPRINT",EDGE,{"disambiguationData":[TD([[subQ9,-1.0]])],"derivedFrom":subQ8}),-1.0]])]});}
            var Q19;
            {var subQ0=sQuery(id+"F4.wireOp",EDGE,"E15.0.4.3");Q19=makeQuery(id+"F4.imprint","IMPRINT",FACE,{"disambiguationData":[TD([[makeQuery(id+"F4.imprint","IMPRINT",EDGE,{"derivedFrom":subQ0}),-1.0]])]});}
            var Q20;
            {var subQ0=sQuery(id+"F4.wireOp",EDGE,"E15.0.3.3");Q20=makeQuery(id+"F4.imprint","IMPRINT",FACE,{"disambiguationData":[TD([[makeQuery(id+"F4.imprint","IMPRINT",EDGE,{"derivedFrom":subQ0}),-1.0]])]});}
            var Q21;
            {var subQ0=sQuery(id+"F4.wireOp",EDGE,"E15.0.3.1");var subQ4=sQuery(id+"F0.wireOp",EDGE,"E0.left");var subQ10=makeQuery(id+"F1.opExtrude","SWEPT_EDGE",EDGE,{"disambiguationData":[OSD([sQuery(id+"F0.wireOp",EDGE,"E0.bottom"),subQ4])]});var subQ11=makeQuery(id+"F4.imprint","INTERSECT",VERTEX,{"derivedFrom":[subQ10,subQ0]});Q21=makeQuery(id+"F4.imprint","IMPRINT",FACE,{"disambiguationData":[TD([[makeQuery(id+"F4.imprint","IMPRINT",EDGE,{"disambiguationData":[TD([[subQ11,-1.0]])],"derivedFrom":subQ10}),-1.0]])]});}
            var Q22;
            {var subQ0=sQuery(id+"F4.wireOp",EDGE,"E15.0.2.1");var subQ1=sQuery(id+"F0.wireOp",EDGE,"E0.left");var subQ3=sQuery(id+"F0.wireOp",EDGE,"E0.bottom");var subQ9=makeQuery(id+"F1.opExtrude","SWEPT_EDGE",EDGE,{"disambiguationData":[OSD([subQ3,subQ1])]});var subQ10=makeQuery(id+"F4.imprint","INTERSECT",VERTEX,{"derivedFrom":[subQ9,subQ0]});Q22=makeQuery(id+"F4.imprint","IMPRINT",FACE,{"disambiguationData":[TD([[makeQuery(id+"F4.imprint","IMPRINT",EDGE,{"disambiguationData":[TD([[subQ10,-1.0]])],"derivedFrom":subQ9}),-1.0]])]});}
            var Q23;
            {var subQ0=sQuery(id+"F4.wireOp",EDGE,"E15.0.2.3");Q23=makeQuery(id+"F4.imprint","IMPRINT",FACE,{"disambiguationData":[TD([[makeQuery(id+"F4.imprint","IMPRINT",EDGE,{"derivedFrom":subQ0}),-1.0]])]});}
            var Q24;
            {var subQ0=sQuery(id+"F4.wireOp",EDGE,"E15.0.1.3");Q24=makeQuery(id+"F4.imprint","IMPRINT",FACE,{"disambiguationData":[TD([[makeQuery(id+"F4.imprint","IMPRINT",EDGE,{"derivedFrom":subQ0}),-1.0]])]});}
            var Q25;
            {var subQ0=sQuery(id+"F4.wireOp",EDGE,"E15.0.1.1");var subQ1=sQuery(id+"F0.wireOp",EDGE,"E0.left");var subQ3=sQuery(id+"F0.wireOp",EDGE,"E0.bottom");var subQ9=makeQuery(id+"F1.opExtrude","SWEPT_EDGE",EDGE,{"disambiguationData":[OSD([subQ3,subQ1])]});var subQ10=makeQuery(id+"F4.imprint","INTERSECT",VERTEX,{"derivedFrom":[subQ9,subQ0]});Q25=makeQuery(id+"F4.imprint","IMPRINT",FACE,{"disambiguationData":[TD([[makeQuery(id+"F4.imprint","IMPRINT",EDGE,{"disambiguationData":[TD([[subQ10,-1.0]])],"derivedFrom":subQ9}),-1.0]])]});}
            var Q26;
            {var subQ0=sQuery(id+"F4.wireOp",EDGE,"E14.bottom");var subQ1=sQuery(id+"F0.wireOp",EDGE,"E0.left");var subQ3=sQuery(id+"F0.wireOp",EDGE,"E0.bottom");var subQ9=makeQuery(id+"F1.opExtrude","SWEPT_EDGE",EDGE,{"disambiguationData":[OSD([subQ3,subQ1])]});var subQ10=makeQuery(id+"F4.imprint","INTERSECT",VERTEX,{"derivedFrom":[subQ9,subQ0]});Q26=makeQuery(id+"F4.imprint","IMPRINT",FACE,{"disambiguationData":[TD([[makeQuery(id+"F4.imprint","IMPRINT",EDGE,{"disambiguationData":[TD([[subQ10,-1.0]])],"derivedFrom":subQ9}),-1.0]])]});}
            var Q27;
            {var subQ0=sQuery(id+"F4.wireOp",EDGE,"E14.right");Q27=makeQuery(id+"F4.imprint","IMPRINT",FACE,{"disambiguationData":[TD([[makeQuery(id+"F4.imprint","IMPRINT",EDGE,{"derivedFrom":subQ0}),-1.0]])]});}
            var Q28;
            {var subQ0=sQuery(id+"F4.wireOp",EDGE,"E17.0.1.0");var subQ2=sQuery(id+"F0.wireOp",EDGE,"E0.left");var subQ8=makeQuery(id+"F1.opExtrude","SWEPT_EDGE",EDGE,{"disambiguationData":[OSD([sQuery(id+"F0.wireOp",EDGE,"E0.bottom"),subQ2])]});var subQ9=makeQuery(id+"F4.imprint","INTERSECT",VERTEX,{"derivedFrom":[subQ8,subQ0]});Q28=makeQuery(id+"F4.imprint","IMPRINT",FACE,{"disambiguationData":[TD([[makeQuery(id+"F4.imprint","IMPRINT",EDGE,{"disambiguationData":[TD([[subQ9,-1.0]])],"derivedFrom":subQ8}),-1.0]])]});}
            var Q29;
            {var subQ0=sQuery(id+"F4.wireOp",EDGE,"E17.0.1.1");Q29=makeQuery(id+"F4.imprint","IMPRINT",FACE,{"disambiguationData":[TD([[makeQuery(id+"F4.imprint","IMPRINT",EDGE,{"derivedFrom":subQ0}),-1.0]])]});}
            var Q30;
            {var subQ0=sQuery(id+"F4.wireOp",EDGE,"E17.0.2.0");var subQ2=sQuery(id+"F0.wireOp",EDGE,"E0.left");var subQ8=makeQuery(id+"F1.opExtrude","SWEPT_EDGE",EDGE,{"disambiguationData":[OSD([sQuery(id+"F0.wireOp",EDGE,"E0.bottom"),subQ2])]});var subQ9=makeQuery(id+"F4.imprint","INTERSECT",VERTEX,{"derivedFrom":[subQ8,subQ0]});Q30=makeQuery(id+"F4.imprint","IMPRINT",FACE,{"disambiguationData":[TD([[makeQuery(id+"F4.imprint","IMPRINT",EDGE,{"disambiguationData":[TD([[subQ9,-1.0]])],"derivedFrom":subQ8}),-1.0]])]});}
            var Q31;
            {var subQ0=sQuery(id+"F4.wireOp",EDGE,"E17.0.2.1");Q31=makeQuery(id+"F4.imprint","IMPRINT",FACE,{"disambiguationData":[TD([[makeQuery(id+"F4.imprint","IMPRINT",EDGE,{"derivedFrom":subQ0}),-1.0]])]});}
            var Q32;
            {var subQ0=sQuery(id+"F4.wireOp",EDGE,"E17.0.3.0");var subQ2=sQuery(id+"F0.wireOp",EDGE,"E0.left");var subQ8=makeQuery(id+"F1.opExtrude","SWEPT_EDGE",EDGE,{"disambiguationData":[OSD([sQuery(id+"F0.wireOp",EDGE,"E0.bottom"),subQ2])]});var subQ9=makeQuery(id+"F4.imprint","INTERSECT",VERTEX,{"derivedFrom":[subQ8,subQ0]});Q32=makeQuery(id+"F4.imprint","IMPRINT",FACE,{"disambiguationData":[TD([[makeQuery(id+"F4.imprint","IMPRINT",EDGE,{"disambiguationData":[TD([[subQ9,-1.0]])],"derivedFrom":subQ8}),-1.0]])]});}
            var Q33;
            {var subQ0=sQuery(id+"F4.wireOp",EDGE,"E17.0.3.1");Q33=makeQuery(id+"F4.imprint","IMPRINT",FACE,{"disambiguationData":[TD([[makeQuery(id+"F4.imprint","IMPRINT",EDGE,{"derivedFrom":subQ0}),-1.0]])]});}
            extrude(context, id + "F5", {"entities" : qUnion([Q0, Q1, Q2, Q3, Q4, Q5, Q6, Q7, Q8, Q9, Q10, Q11, Q12, Q13, Q14, Q15, Q16, Q17, Q18, Q19, Q20, Q21, Q22, Q23, Q24, Q25, Q26, Q27, Q28, Q29, Q30, Q31, Q32, Q33]), "operationType" : NewBodyOperationType.REMOVE, "oppositeDirection" : true, "depth" : 2 * mm, "offsetDistance" : 25 * mm, "hasDraft" : true, "draftAngle" : 45 * degree, "draftPullDirection" : true});
        }
    });
